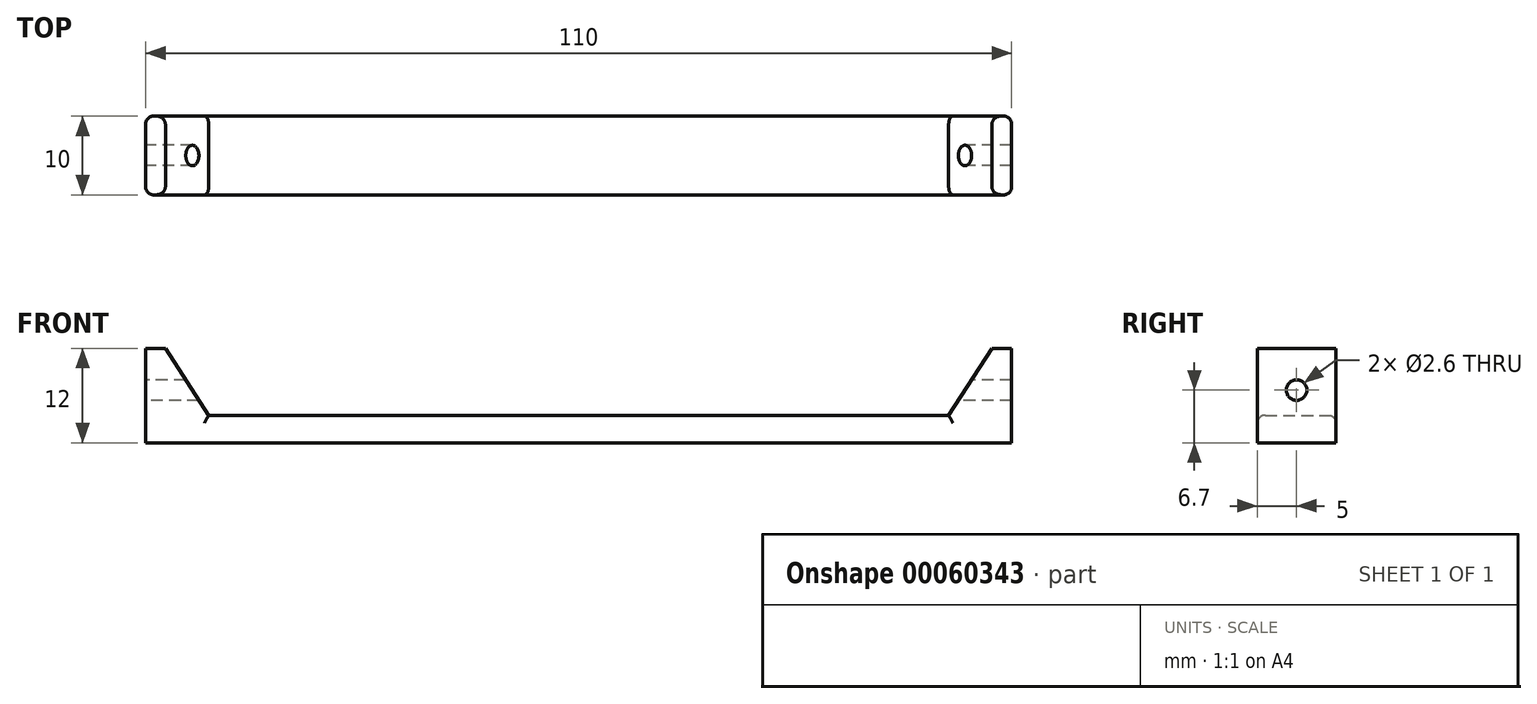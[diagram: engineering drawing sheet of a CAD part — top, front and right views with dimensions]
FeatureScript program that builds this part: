
annotation { "Feature Type Name" : "Feature", "Feature Type Description" : "" }
export const myFeature = defineFeature(function(context is Context, id is Id, definition is map)
    precondition{}
    {
        {
            var Q0;
            Q0=qCreatedBy(makeId("Front.planeOp"),FACE);
            var sketch = newSketch(context, id + "F0", { "sketchPlane" : qUnion([Q0])});
            skLineSegment(sketch, "E0", {"start": v(-55, 0) * mm, "end": v(-55, 12) * mm});
            skLineSegment(sketch, "E1", {"start": v(-55, 12) * mm, "end": v(-52.5, 12) * mm});
            skLineSegment(sketch, "E2", {"start": v(-52.5, 12) * mm, "end": v(-47, 3.5) * mm});
            skLineSegment(sketch, "E3", {"start": v(-47, 3.5) * mm, "end": v(0, 3.5) * mm});
            skLineSegment(sketch, "E4", {"start": v(-55, 0) * mm, "end": v(0, 0) * mm});
            skLineSegment(sketch, "E5.MirrorCS", {"start": v(55, 12) * mm, "end": v(52.5, 12) * mm});
            skLineSegment(sketch, "E6.MirrorCS", {"start": v(52.5, 12) * mm, "end": v(47, 3.5) * mm});
            skLineSegment(sketch, "E7.MirrorCS", {"start": v(55, 0) * mm, "end": v(55, 12) * mm});
            skLineSegment(sketch, "E8.MirrorCS", {"start": v(47, 3.5) * mm, "end": v(0, 3.5) * mm});
            skLineSegment(sketch, "E9.MirrorCS", {"start": v(55, 0) * mm, "end": v(0, 0) * mm});
            skSolve(sketch);
        }
        {
            var Q0;
            Q0=makeQuery(id+"F0.imprint","IMPRINT",FACE,{"disambiguationData":[TD([[makeQuery(id+"F0.imprint","IMPRINT",EDGE,{"derivedFrom":sQuery(id+"F0.wireOp",EDGE,"E0")}),-1.0]])]});
            extrude(context, id + "F1", {"entities" : qUnion([Q0]), "endBound" : BoundingType.SYMMETRIC, "depth" : 10 * mm});
        }
        {
            var Q0;
            Q0=makeQuery(id+"F1.opExtrude","SWEPT_FACE",FACE,{"disambiguationData":[OSD([sQuery(id+"F0.wireOp",EDGE,"E0")])]});
            var sketch = newSketch(context, id + "F2", { "sketchPlane" : qUnion([Q0])});
            skCircle(sketch, "E10", {"center": v(0, 6.7) * mm, "radius": 1.3 * mm});
            skSolve(sketch);
        }
        {
            var Q0;
            Q0 = qSketchRegion(id + "F2", true);
            var Q1;
            Q1=makeQuery(id+"F1.opExtrude","SWEPT_FACE",FACE,{"disambiguationData":[OSD([sQuery(id+"F0.wireOp",EDGE,"E7.MirrorCS")])]});
            extrude(context, id + "F3", {"entities" : qUnion([Q0]), "operationType" : NewBodyOperationType.REMOVE, "endBound" : BoundingType.UP_TO_SURFACE, "oppositeDirection" : true, "endBoundEntityFace" : qUnion([Q1]), "depth" : 25 * mm});
        }
        {
            var Q0;
            Q0=makeQuery(id+"F1.opExtrude","CAP_EDGE",EDGE,{"disambiguationData":[OSD([sQuery(id+"F0.wireOp",EDGE,"E2")])],"isStart":true});
            var Q1;
            Q1=makeQuery(id+"F1.opExtrude","CAP_EDGE",EDGE,{"disambiguationData":[OSD([sQuery(id+"F0.wireOp",EDGE,"E2")])],"isStart":false});
            var Q2;
            Q2=makeQuery(id+"F1.opExtrude","CAP_EDGE",EDGE,{"disambiguationData":[OSD([sQuery(id+"F0.wireOp",EDGE,"E3"),sQuery(id+"F0.wireOp",EDGE,"E8.MirrorCS")])],"isStart":false});
            var Q3;
            Q3=makeQuery(id+"F1.opExtrude","CAP_EDGE",EDGE,{"disambiguationData":[OSD([sQuery(id+"F0.wireOp",EDGE,"E3"),sQuery(id+"F0.wireOp",EDGE,"E8.MirrorCS")])],"isStart":true});
            var Q4;
            Q4=makeQuery(id+"F1.opExtrude","CAP_EDGE",EDGE,{"disambiguationData":[OSD([sQuery(id+"F0.wireOp",EDGE,"E6.MirrorCS")])],"isStart":true});
            var Q5;
            Q5=makeQuery(id+"F1.opExtrude","CAP_EDGE",EDGE,{"disambiguationData":[OSD([sQuery(id+"F0.wireOp",EDGE,"E6.MirrorCS")])],"isStart":false});
            var Q6;
            Q6=makeQuery(id+"F1.opExtrude","CAP_EDGE",EDGE,{"disambiguationData":[OSD([sQuery(id+"F0.wireOp",EDGE,"E0")])],"isStart":false});
            var Q7;
            Q7=makeQuery(id+"F1.opExtrude","CAP_EDGE",EDGE,{"disambiguationData":[OSD([sQuery(id+"F0.wireOp",EDGE,"E0")])],"isStart":true});
            var Q8;
            Q8=makeQuery(id+"F1.opExtrude","CAP_EDGE",EDGE,{"disambiguationData":[OSD([sQuery(id+"F0.wireOp",EDGE,"E7.MirrorCS")])],"isStart":false});
            var Q9;
            Q9=makeQuery(id+"F1.opExtrude","CAP_EDGE",EDGE,{"disambiguationData":[OSD([sQuery(id+"F0.wireOp",EDGE,"E7.MirrorCS")])],"isStart":true});
            fillet(context, id + "F4", {"entities" : qUnion([Q0, Q1, Q2, Q3, Q4, Q5, Q6, Q7, Q8, Q9]), "radius" : 1 * mm, "tangentPropagation" : true, "allowEdgeOverflow" : false});
        }
    });
